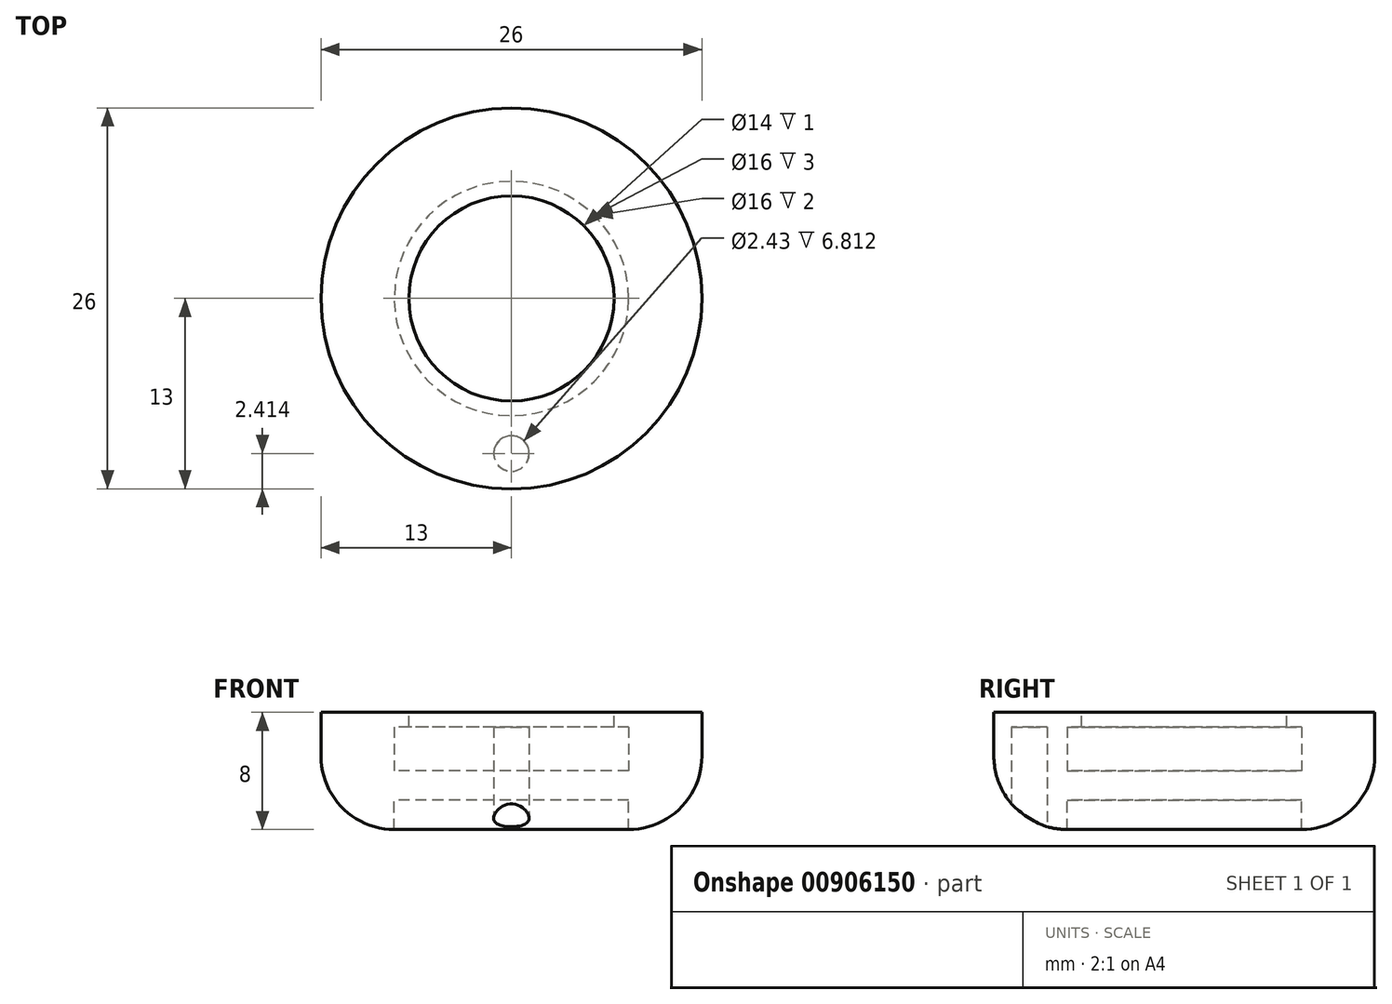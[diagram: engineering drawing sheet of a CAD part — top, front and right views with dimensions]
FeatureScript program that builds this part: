
annotation { "Feature Type Name" : "Feature", "Feature Type Description" : "" }
export const myFeature = defineFeature(function(context is Context, id is Id, definition is map)
    precondition{}
    {
        {
            var Q0;
            Q0=qCreatedBy(makeId("Top.planeOp"),FACE);
            var sketch = newSketch(context, id + "F0", { "sketchPlane" : qUnion([Q0])});
            skCircle(sketch, "E0", {"center": v(0, 0) * mm, "radius": 7 * mm});
            skCircle(sketch, "E1", {"center": v(0, 0) * mm, "radius": 8 * mm});
            skCircle(sketch, "E2", {"center": v(0, 0) * mm, "radius": 13 * mm});
            skCircle(sketch, "E3", {"center": v(0, -10.59) * mm, "radius": 1.21 * mm});
            skSolve(sketch);
        }
        {
            var Q0;
            Q0=makeQuery(id+"F0.imprint","IMPRINT",FACE,{"disambiguationData":[TD([[makeQuery(id+"F0.imprint","IMPRINT",EDGE,{"derivedFrom":sQuery(id+"F0.wireOp",EDGE,"E0")}),1.0]])]});
            var Q1;
            Q1=makeQuery(id+"F0.imprint","IMPRINT",FACE,{"disambiguationData":[TD([[makeQuery(id+"F0.imprint","IMPRINT",EDGE,{"derivedFrom":sQuery(id+"F0.wireOp",EDGE,"E0")}),-1.0]])]});
            var Q2;
            Q2=makeQuery(id+"F0.imprint","IMPRINT",FACE,{"disambiguationData":[TD([[makeQuery(id+"F0.imprint","IMPRINT",EDGE,{"derivedFrom":sQuery(id+"F0.wireOp",EDGE,"E1")}),-1.0]])]});
            extrude(context, id + "F1", {"entities" : qUnion([Q0, Q1, Q2]), "depth" : 2 * mm});
        }
        {
            var Q0;
            Q0=makeQuery(id+"F0.imprint","IMPRINT",FACE,{"disambiguationData":[TD([[makeQuery(id+"F0.imprint","IMPRINT",EDGE,{"derivedFrom":sQuery(id+"F0.wireOp",EDGE,"E1")}),-1.0]])]});
            extrude(context, id + "F2", {"entities" : qUnion([Q0]), "operationType" : NewBodyOperationType.ADD, "depth" : 6 * mm});
        }
        {
            var Q0;
            Q0=makeQuery(id+"F2.opExtrude","CAP_FACE",FACE,{"disambiguationData":[OSD([sQuery(id+"F0.wireOp",EDGE,"E1"),sQuery(id+"F0.wireOp",EDGE,"E2")])],"isStart":false});
            cPlane(context, id + "F3", {"entities" : qUnion([Q0]), "cplaneType" : CPlaneType.OFFSET, "offset" : 0 * mm, "width" : 150 * mm, "height" : 150 * mm});
        }
        {
            var Q0;
            Q0=qCreatedBy(id+"F3.planeOp",FACE);
            var sketch = newSketch(context, id + "F4", { "sketchPlane" : qUnion([Q0])});
            skCircle(sketch, "E4", {"center": v(0, 0) * mm, "radius": 8 * mm});
            skCircle(sketch, "E5", {"center": v(0, 0) * mm, "radius": 7 * mm});
            skCircle(sketch, "E6", {"center": v(0, 0) * mm, "radius": 13 * mm});
            skSolve(sketch);
        }
        {
            var Q0;
            Q0=qSketchRegion(id+"F4",true);
            var Q1;
            Q1=makeQuery(id+"F4.imprint","IMPRINT",FACE,{"disambiguationData":[TD([[makeQuery(id+"F4.imprint","IMPRINT",EDGE,{"derivedFrom":sQuery(id+"F4.wireOp",EDGE,"E4")}),1.0]])]});
            extrude(context, id + "F5", {"entities" : qUnion([Q0, Q1]), "operationType" : NewBodyOperationType.ADD, "oppositeDirection" : true, "depth" : 1 * mm});
        }
        {
            var Q0;
            Q0=makeQuery(id+"F2.opExtrude","CAP_FACE",FACE,{"disambiguationData":[OSD([sQuery(id+"F0.wireOp",EDGE,"E1"),sQuery(id+"F0.wireOp",EDGE,"E2")])],"isStart":true});
            var Q1;
            Q1=makeQuery(id+"F0.imprint","IMPRINT",FACE,{"disambiguationData":[TD([[makeQuery(id+"F0.imprint","IMPRINT",EDGE,{"derivedFrom":sQuery(id+"F0.wireOp",EDGE,"E0")}),1.0]])]});
            extrude(context, id + "F6", {"entities" : qUnion([Q0, Q1]), "operationType" : NewBodyOperationType.ADD, "depth" : 1 * mm});
        }
        {
            var Q0;
            Q0=qSketchRegion(id+"F0",true);
            extrude(context, id + "F7", {"entities" : qUnion([Q0]), "operationType" : NewBodyOperationType.ADD, "oppositeDirection" : true, "depth" : 2 * mm});
        }
        {
            var Q0;
            Q0=makeQuery(id+"F7.opExtrude","CAP_EDGE",EDGE,{"disambiguationData":[OSD([sQuery(id+"F0.wireOp",EDGE,"E2")])],"isStart":false});
            fillet(context, id + "F8", {"entities" : qUnion([Q0]), "radius" : 5 * mm, "tangentPropagation" : true, "allowEdgeOverflow" : false});
        }
    });
